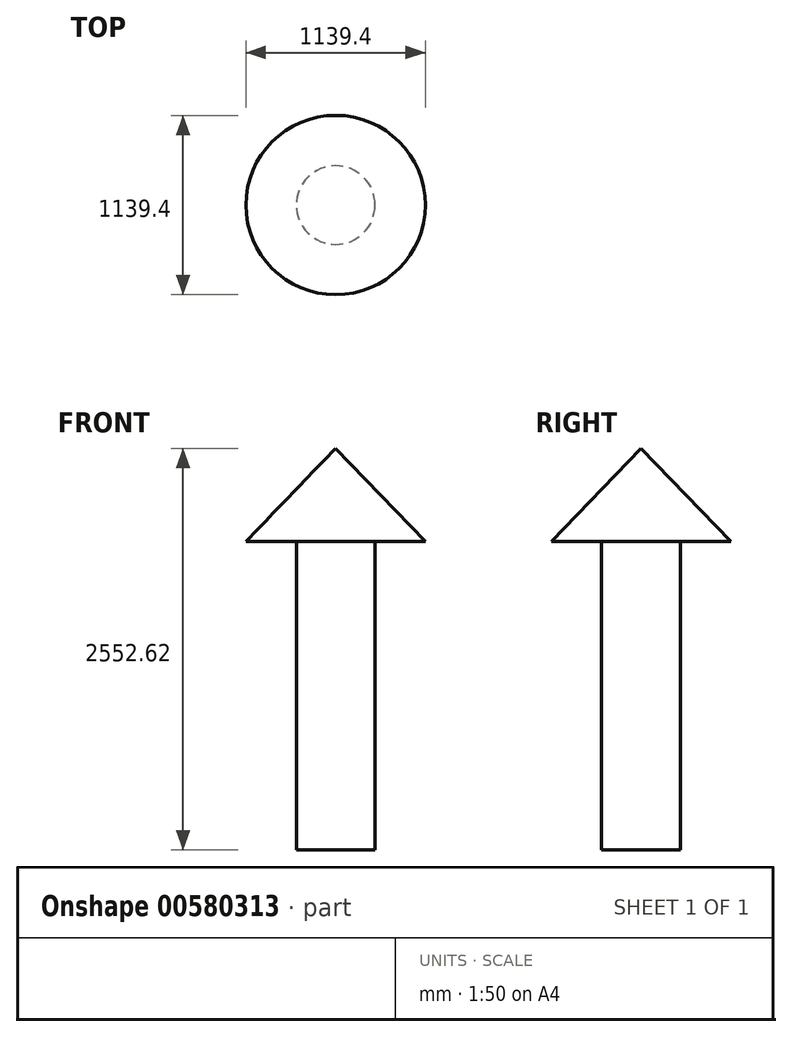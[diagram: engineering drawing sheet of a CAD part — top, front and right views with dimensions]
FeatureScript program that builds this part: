
annotation { "Feature Type Name" : "Feature", "Feature Type Description" : "" }
export const myFeature = defineFeature(function(context is Context, id is Id, definition is map)
    precondition{}
    {
        {
            var Q0;
            Q0=qCreatedBy(makeId("Top.planeOp"),FACE);
            var sketch = newSketch(context, id + "F0", { "sketchPlane" : qUnion([Q0])});
            skCircle(sketch, "E0", {"center": v(0, 0) * mm, "radius": 250 * mm});
            skSolve(sketch);
        }
        {
            var Q0;
            Q0 = qSketchRegion(id + "F0", true);
            extrude(context, id + "F1", {"entities" : qUnion([Q0]), "depth" : 1960 * mm, "offsetDistance" : 25 * mm});
        }
        {
            var Q0;
            Q0=qCreatedBy(makeId("Front.planeOp"),FACE);
            var sketch = newSketch(context, id + "F2", { "sketchPlane" : qUnion([Q0])});
            skLineSegment(sketch, "E1", {"start": v(0, 1960) * mm, "end": v(0, 2552.62) * mm});
            skLineSegment(sketch, "E2", {"start": v(0, 1960) * mm, "end": v(-569.7, 1960) * mm});
            skLineSegment(sketch, "E3", {"start": v(-569.7, 1960) * mm, "end": v(0, 2552.62) * mm});
            skSolve(sketch);
        }
        {
            var Q0;
            Q0 = qSketchRegion(id + "F2", true);
            var Q1;
            Q1=sQuery(id+"F2.wireOp",EDGE,"E1");
            revolve(context, id + "F3", {"operationType" : NewBodyOperationType.ADD, "entities" : qUnion([Q0]), "axis" : qUnion([Q1]), "revolveType" : RevolveType.FULL});
        }
    });
